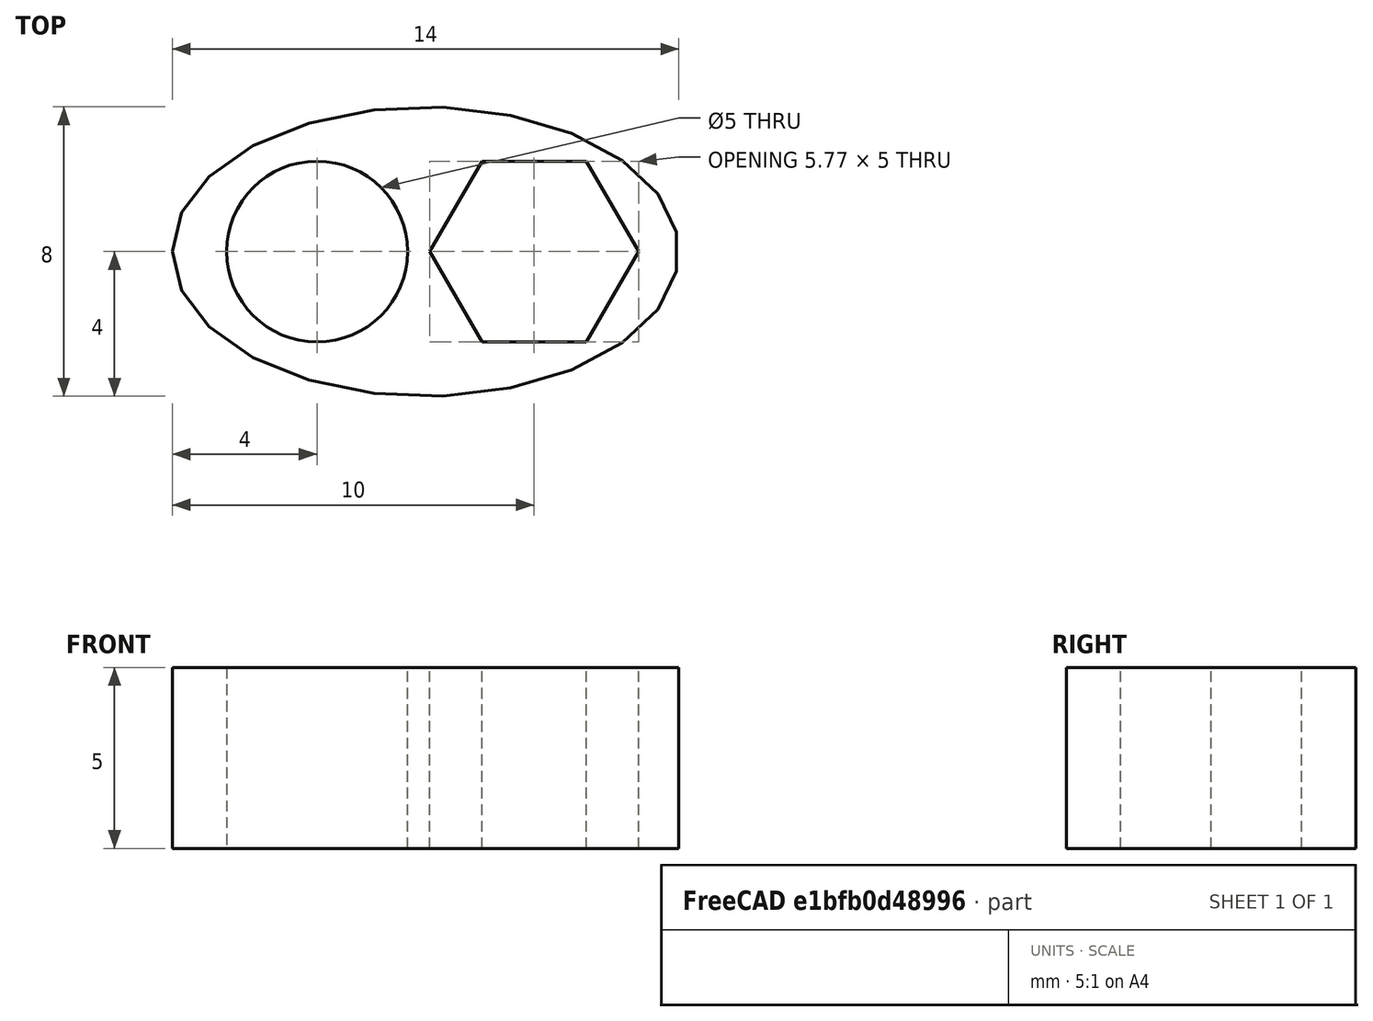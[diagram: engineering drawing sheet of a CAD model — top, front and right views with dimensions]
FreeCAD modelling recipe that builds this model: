
FCSTD DOCUMENT  (FreeCAD 0.21R33771 (Git))
Label: mount
License: All rights reserved
LicenseURL: https://en.wikipedia.org/wiki/All_rights_reserved
objects: PartDesign::Body×1, App::Part×1, Sketcher::SketchObject×1, Part::Extrusion×1
note: 3 computed .brp shape members not serialized (recipe doc carries the construction recipe); baked Part::Feature solids carry a one-line shape summary decoded from their .brp

FEATURE [PartDesign::Body] Body
  Origin = -> Origin001
FEATURE [App::Part] Part
  Group = -> [Body]
  Origin = -> Origin
FEATURE [Sketcher::SketchObject] Sketch
  FullyConstrained = true
  MapMode = 2
  Support = -> [Part]
  sketch-geometry (13):
    g0: Circle CenterX=0 CenterY=0 CenterZ=0 NormalX=0 NormalY=0 NormalZ=1 AngleXU=0 Radius=2.5
    g1: LineSegment StartX=7.44338 StartY=-2.5 StartZ=0 EndX=8.88675 EndY=0 EndZ=0
    g2: LineSegment StartX=8.88675 StartY=0 StartZ=0 EndX=7.44338 EndY=2.5 EndZ=0
    g3: LineSegment StartX=7.44338 StartY=2.5 StartZ=0 EndX=4.55662 EndY=2.5 EndZ=0
    g4: LineSegment StartX=4.55662 StartY=2.5 StartZ=0 EndX=3.11325 EndY=0 EndZ=0
    g5: LineSegment StartX=3.11325 StartY=0 StartZ=0 EndX=4.55662 EndY=-2.5 EndZ=0
    g6: LineSegment StartX=4.55662 StartY=-2.5 StartZ=0 EndX=7.44338 EndY=-2.5 EndZ=0
    g7: Circle CenterX=6 CenterY=0 CenterZ=0 NormalX=0 NormalY=0 NormalZ=1 AngleXU=0 Radius=2.88675
    g8: Ellipse CenterX=3 CenterY=0 CenterZ=0 NormalX=0 NormalY=0 NormalZ=1 MajorRadius=7 MinorRadius=4 AngleXU=3.14159
    g9: LineSegment StartX=-4 StartY=0 StartZ=0 EndX=10 EndY=0 EndZ=0
    g10: LineSegment StartX=3 StartY=-4 StartZ=0 EndX=3 EndY=4 EndZ=0
    g11: GeomPoint X=-2.74456 Y=0 Z=0
    g12: GeomPoint X=8.74456 Y=0 Z=0
  constraints (26):
    c: DistanceX(g0,g-1) = 0
    c: DistanceY(g0) = 0
    c: Diameter(g0) = 5
    c: Coincident(g1,g2)
    c: Coincident(g2,g3)
    c: Coincident(g3,g4)
    c: Coincident(g4,g5)
    c: Coincident(g5,g6)
    c: Coincident(g6,g1)
    c: Equal(g1, g2-g6) x5
    c: PointOnObject(g1,g7)
    c: PointOnObject(g2,g7)
    c: PointOnObject(g3,g7)
    c: PointOnObject(g4,g7)
    c: PointOnObject(g5,g7)
    c: PointOnObject(g6,g7)
    c: Parallel(g3,g-1)
    c: DistanceY(g0,g7) = 0
    c: DistanceX(g0,g7) = 6
    c: Distance(g3,g5) = 5
    c: InternalAlignment(g9-g12 -> g8) x4
    c: DistanceY(g0,g8) = 0
    c: Parallel(g9,g-1)
    c: DistanceX(g9,g9) = 14
    c: DistanceX(g0,g8) = 3
    c: DistanceY(g10,g10) = 8
FEATURE [Part::Extrusion] Extrude
  Base = -> Sketch
  Dir = (0,0,1)
  DirMode = 2
  FaceMakerClass = Part::FaceMakerBullseye
  LengthFwd = 5
  LengthRev = 0
  Solid = true
  Symmetric = false
